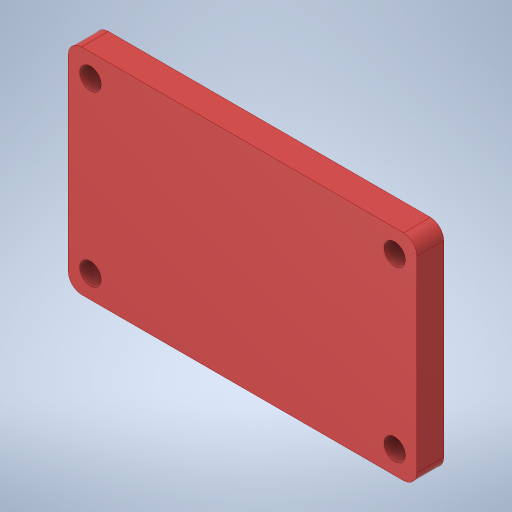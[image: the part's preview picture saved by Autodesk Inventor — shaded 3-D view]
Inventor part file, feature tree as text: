
AUTODESK INVENTOR PART (.ipt)
format: ipt  version: 2023.3 (Build 273359000, 359)  size: 223,744 bytes
history: native  units: in
note: dims shown in document units (in); Inventor stores cm internally (conversion verified against a paired STEP export)
features: sketch x2, extrude x1, fillet x1, hole x1
ambient origin geometry x8: Origin, YZ Plane, XZ Plane, XY Plane, X Axis, Y Axis, Z Axis, Center Point
bodies: Solid1 (feature_tree)
feature tree (5):
  extrude  "Extrusion1"  Depth=3.25in
  fillet  "Fillet1"  Radius=0.25in
  hole  "Hole1"  [1 undecoded]
  sketch  "Sketch1"  dims[d0=2.0in d1=3.25in d2=0.25in d3=0.0in]
  sketch  "Sketch2"  dims[d4=0.125in d5=2.835in d6=1.575in d7=0.201in d8=0.75in d9=0.385in d10=0.25in d11=0.5635in d12=1.0in d13=0.8108in]
note: 1 required parameter value undecoded (feature->parameter linkage not recoverable at this tier; creation-order binding heuristic only, values carry confidence <= 0.55)
